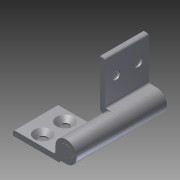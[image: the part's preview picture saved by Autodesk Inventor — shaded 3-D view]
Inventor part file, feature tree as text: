
AUTODESK INVENTOR PART (.ipt)
format: ipt  version: 2011 SP1 (Build 150282100, 282)  size: 172,544 bytes
history: native  units: mm
features: other x42, sketch x8, extrude x4, hole x4
ambient origin geometry x8: Origin, YZ Plane, XZ Plane, XY Plane, X Axis, Y Axis, Z Axis, Center Point
bodies: Solid1 (feature_tree)
feature tree (58):
  extrude  "Extrusion1"  Depth=85.5mm TaperAngle=0.0deg
  extrude  "Extrusion2"  Depth=41.25mm TaperAngle=0.0deg
  extrude  "Extrusion3"  [1 undecoded]
  extrude  "Extrusion4"  [1 undecoded]
  hole  "Drilling 1"  [1 undecoded]
  hole  "Drilling 2"  [1 undecoded]
  hole  "Drilling 3"  [1 undecoded]
  hole  "Drilling 4"  [1 undecoded]
  other  "side_2a_XY"
  other  "side_2a_YZ"
  other  "side_2a_ZX"
  other  "side_2a_X"
  other  "side_2a_Y"
  other  "side_2a_Z"
  other  "side_2a_Center"
  other  "side_2b_XY"
  other  "side_2b_YZ"
  other  "side_2b_ZX"
  other  "side_2b_X"
  other  "side_2b_Y"
  other  "side_2b_Z"
  other  "side_2b_Center"
  other  "side_1b_XY"
  other  "side_1b_YZ"
  other  "side_1b_ZX"
  other  "side_1b_X"
  other  "side_1b_Y"
  other  "side_1b_Z"
  other  "side_1b_Center"
  other  "side_3b_XY"
  other  "side_3b_YZ"
  other  "side_3b_ZX"
  other  "side_3b_X"
  other  "side_3b_Y"
  other  "side_3b_Z"
  other  "side_3b_Center"
  other  "side_1a_XY"
  other  "side_1a_YZ"
  other  "side_1a_ZX"
  other  "side_1a_X"
  other  "side_1a_Y"
  other  "side_1a_Z"
  other  "side_1a_Center"
  other  "side_3a_XY"
  other  "side_3a_YZ"
  other  "side_3a_ZX"
  other  "side_3a_X"
  other  "side_3a_Y"
  other  "side_3a_Z"
  other  "side_3a_Center"
  sketch  "Skizze_34"  dims[d22=8.0mm d23=6.0mm d24=16.0mm d25=2.0mm d26=15.707963mm d27=5.0mm d28=0.0mm]
  sketch  "Skizze_35"  dims[d29=8.0mm d30=6.0mm d31=16.0mm d32=2.0mm d33=15.707963mm d34=5.0mm d35=0.0mm]
  sketch  "Skizze_36"
  sketch  "Skizze_37"
  sketch  "Sketch5"  dims[d0=2.5mm d1=0.0mm d2=85.5mm d3=0.0mm]
  sketch  "Sketch6"  dims[d4=41.25mm d5=0.0mm d6=41.25mm d7=0.0mm]
  sketch  "Sketch7"  dims[d8=8.0mm d9=6.0mm d10=16.0mm d11=2.0mm d12=15.707963mm d13=5.0mm d14=0.0mm]
  sketch  "Sketch8"  dims[d15=8.0mm d16=6.0mm d17=16.0mm d18=2.0mm d19=15.707963mm d20=5.0mm d21=0.0mm]
note: 6 required parameter values undecoded (feature->parameter linkage not recoverable at this tier; creation-order binding heuristic only, values carry confidence <= 0.55)
